# Revit family: Showerhead-American_Standard-Fluent-1660604.002
name_source: partatom
category: Plumbing Fixtures
units: mm (PartAtom-declared; Revit-internal decimal feet)

## family parameters
Always vertical = No
Cut with Voids When Loaded = No
OmniClass Number = 23.45.05.14.17
OmniClass Title = Showers
Part Type = Normal
Room Calculation Point = No
Round Connector Dimension = Use Diameter
Shared = Yes
Work Plane-Based = No

## types (1)
- 1660604.002
    1660240 - Standard Shower Arm and Flange = No
    1660241 - Modern Shower Arm and Flange = No
    Assembly Code = D2010700
    CW Connection = No
    CWFU = 3
    Description = Fluent® 7-Inch 2.5 gpm/9.5 L/min Fixed Showerhead
    Finish = Brass-American Standard-002-Polished Chrome
    Flow Rate = 2.5 gpm/9.5 L/min
    HW Connection = No
    HWFU = 3
    Height = 3 5/32"
    Manufacturer = American Standard
    Material = Brass-American Standard-002-Polished Chrome
    Model = 1660604.002
    Product Documentation Link = https://americanstandard.box.com
    Product Page URL = https://www.americanstandard-us.com
    Revised Date = 11/17/2022
    Tempered Water Connection = Yes
    Tempered Water Connection Diameter = 1/2"
    Tempered Water Connection Radius = 1/4"
    URL = http://www.americanstandard-us.com
    Vent Connection = No
    WFU = 4
    Waste Connection = No
    Width = 7 1/16"

## geometry (parser evidence)
native form markers: Sweep x2
no freeform markers — native parametric forms only
